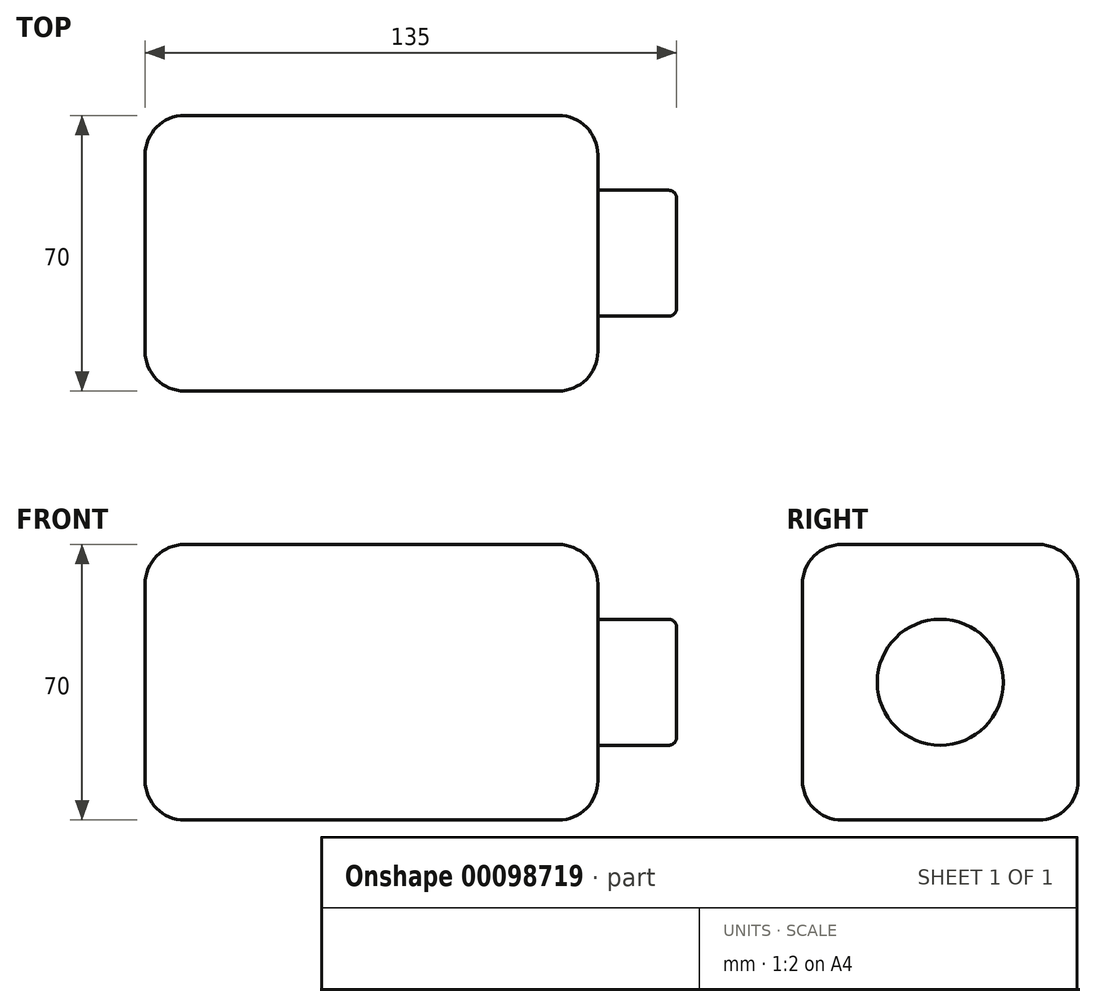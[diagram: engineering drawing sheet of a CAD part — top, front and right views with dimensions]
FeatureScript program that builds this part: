
annotation { "Feature Type Name" : "Feature", "Feature Type Description" : "" }
export const myFeature = defineFeature(function(context is Context, id is Id, definition is map)
    precondition{}
    {
        {
            var Q0;
            Q0=qCreatedBy(makeId("Right.planeOp"),FACE);
            var sketch = newSketch(context, id + "F0", { "sketchPlane" : qUnion([Q0])});
            skLineSegment(sketch, "E0.bottom", {"start": v(35, 35) * mm, "end": v(-35, 35) * mm});
            skLineSegment(sketch, "E0.top", {"start": v(35, -35) * mm, "end": v(-35, -35) * mm});
            skLineSegment(sketch, "E0.left", {"start": v(35, 35) * mm, "end": v(35, -35) * mm});
            skLineSegment(sketch, "E0.right", {"start": v(-35, 35) * mm, "end": v(-35, -35) * mm});
            skPoint(sketch, "E0.middle", {"position": v(0, 0) * mm});
            skSolve(sketch);
        }
        {
            var Q0;
            Q0 = qSketchRegion(id + "F0", true);
            extrude(context, id + "F1", {"entities" : qUnion([Q0]), "depth" : 115 * mm, "symmetric" : true});
        }
        {
            var Q0;
            Q0=makeQuery(id+"F1.opExtrude","CAP_EDGE",EDGE,{"disambiguationData":[OSD([sQuery(id+"F0.wireOp",EDGE,"E0.right")])],"isStart":false});
            var Q1;
            Q1=makeQuery(id+"F1.opExtrude","CAP_EDGE",EDGE,{"disambiguationData":[OSD([sQuery(id+"F0.wireOp",EDGE,"E0.bottom")])],"isStart":false});
            var Q2;
            Q2=makeQuery(id+"F1.opExtrude","SWEPT_EDGE",EDGE,{"disambiguationData":[OSD([sQuery(id+"F0.wireOp",EDGE,"E0.bottom"),sQuery(id+"F0.wireOp",EDGE,"E0.right")])]});
            var Q3;
            Q3=makeQuery(id+"F1.opExtrude","CAP_EDGE",EDGE,{"disambiguationData":[OSD([sQuery(id+"F0.wireOp",EDGE,"E0.left")])],"isStart":false});
            var Q4;
            Q4=makeQuery(id+"F1.opExtrude","SWEPT_EDGE",EDGE,{"disambiguationData":[OSD([sQuery(id+"F0.wireOp",EDGE,"E0.bottom"),sQuery(id+"F0.wireOp",EDGE,"E0.left")])]});
            var Q5;
            Q5=makeQuery(id+"F1.opExtrude","CAP_EDGE",EDGE,{"disambiguationData":[OSD([sQuery(id+"F0.wireOp",EDGE,"E0.left")])],"isStart":true});
            var Q6;
            Q6=makeQuery(id+"F1.opExtrude","CAP_EDGE",EDGE,{"disambiguationData":[OSD([sQuery(id+"F0.wireOp",EDGE,"E0.right")])],"isStart":true});
            var Q7;
            Q7=makeQuery(id+"F1.opExtrude","SWEPT_EDGE",EDGE,{"disambiguationData":[OSD([sQuery(id+"F0.wireOp",EDGE,"E0.top"),sQuery(id+"F0.wireOp",EDGE,"E0.right")])]});
            var Q8;
            Q8=makeQuery(id+"F1.opExtrude","CAP_EDGE",EDGE,{"disambiguationData":[OSD([sQuery(id+"F0.wireOp",EDGE,"E0.top")])],"isStart":false});
            var Q9;
            Q9=makeQuery(id+"F1.opExtrude","CAP_EDGE",EDGE,{"disambiguationData":[OSD([sQuery(id+"F0.wireOp",EDGE,"E0.top")])],"isStart":true});
            var Q10;
            Q10=makeQuery(id+"F1.opExtrude","CAP_EDGE",EDGE,{"disambiguationData":[OSD([sQuery(id+"F0.wireOp",EDGE,"E0.bottom")])],"isStart":true});
            var Q11;
            Q11=makeQuery(id+"F1.opExtrude","SWEPT_EDGE",EDGE,{"disambiguationData":[OSD([sQuery(id+"F0.wireOp",EDGE,"E0.top"),sQuery(id+"F0.wireOp",EDGE,"E0.left")])]});
            fillet(context, id + "F2", {"entities" : qUnion([Q0, Q1, Q2, Q3, Q4, Q5, Q6, Q7, Q8, Q9, Q10, Q11]), "radius" : 10 * mm, "tangentPropagation" : true, "allowEdgeOverflow" : false});
        }
        {
            var Q0;
            Q0=qCreatedBy(makeId("Right.planeOp"),FACE);
            var sketch = newSketch(context, id + "F3", { "sketchPlane" : qUnion([Q0])});
            skCircle(sketch, "E1", {"center": v(0, 0) * mm, "radius": 16 * mm});
            skSolve(sketch);
        }
        {
            var Q0;
            Q0 = qSketchRegion(id + "F3", true);
            extrude(context, id + "F4", {"entities" : qUnion([Q0]), "depth" : 20 * mm});
        }
        {
            var Q0;
            Q0=makeQuery(id+"F4.opExtrude","SWEPT_BODY",BODY,{"disambiguationData":[OSD([sQuery(id+"F3.wireOp",EDGE,"E1")])]});
            var Q1;
            Q1=qCreatedBy(makeId("Right.planeOp"),FACE);
            transform(context, id + "F5", {"entities" : qUnion([Q0]), "transformType" : TransformType.TRANSLATION_DISTANCE, "transformDirection" : qUnion([Q1]), "distance" : 57.5 * mm, "makeCopy" : false});
        }
        {
            var Q0;
            Q0=makeQuery(id+"F4.opExtrude","CAP_EDGE",EDGE,{"disambiguationData":[OSD([sQuery(id+"F3.wireOp",EDGE,"E1")])],"isStart":false});
            fillet(context, id + "F6", {"entities" : qUnion([Q0]), "radius" : 2 * mm, "tangentPropagation" : true, "allowEdgeOverflow" : false});
        }
    });
